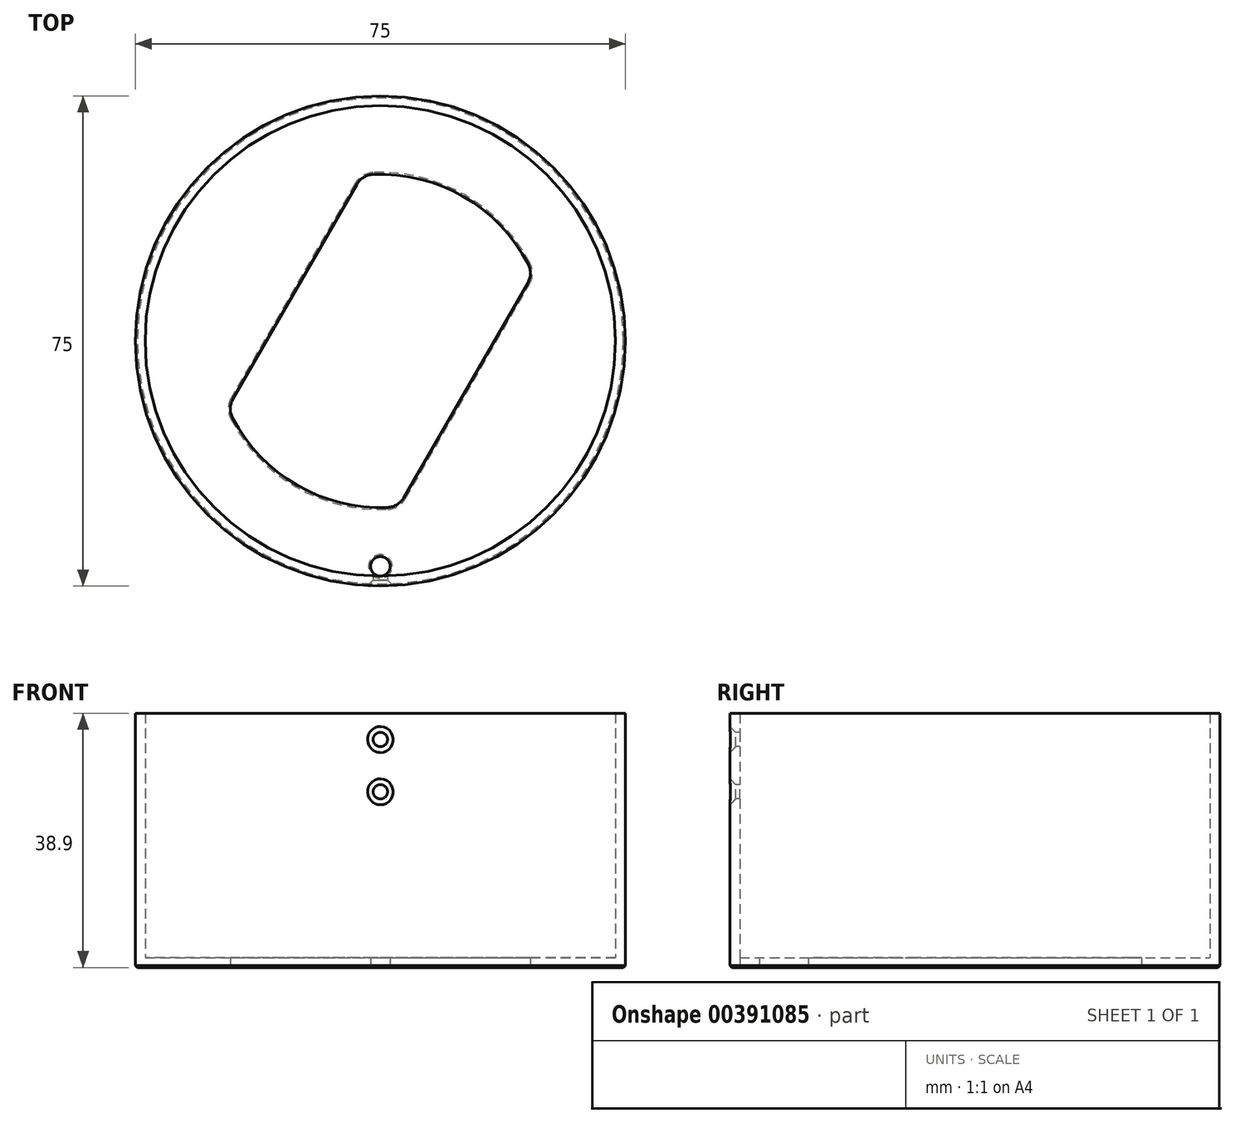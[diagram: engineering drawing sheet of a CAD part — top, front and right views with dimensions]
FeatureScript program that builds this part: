
annotation { "Feature Type Name" : "Feature", "Feature Type Description" : "" }
export const myFeature = defineFeature(function(context is Context, id is Id, definition is map)
    precondition{}
    {
        {
            var Q0;
            Q0=qCreatedBy(makeId("Top.planeOp"),FACE);
            var sketch = newSketch(context, id + "F0", { "sketchPlane" : qUnion([Q0])});
            skCircle(sketch, "E0", {"center": v(0, 0) * mm, "radius": 37.5 * mm});
            skCircle(sketch, "E1", {"center": v(0, 0) * mm, "radius": 36 * mm});
            skArc(sketch, "E2", {"start": v(-22.63, -11.76) * mm, "mid": v(-12.75, -22.08) * mm, "end": v(1.13, -25.48) * mm});
            skLineSegment(sketch, "E3", {"start": v(-29.66, -51.37) * mm, "end": v(37.36, 64.7) * mm, "construction": true});
            skLineSegment(sketch, "E4", {"start": v(-3.6, 23.98) * mm, "end": v(-22.56, -8.88) * mm});
            skLineSegment(sketch, "E5", {"start": v(3.6, -23.98) * mm, "end": v(22.56, 8.88) * mm});
            skArc(sketch, "E6.trimOffspring", {"start": v(22.63, 11.76) * mm, "mid": v(12.75, 22.08) * mm, "end": v(-1.13, 25.48) * mm});
            skPoint(sketch, "E7.visualSharp", {"position": v(-2.8, 25.35) * mm});
            skArc(sketch, "E7.filletArc", {"start": v(-1.13, 25.48) * mm, "mid": v(-2.55, 25.04) * mm, "end": v(-3.6, 23.98) * mm});
            skPoint(sketch, "E8.visualSharp", {"position": v(23.35, 10.25) * mm});
            skArc(sketch, "E8.filletArc", {"start": v(22.56, 8.88) * mm, "mid": v(22.96, 10.31) * mm, "end": v(22.63, 11.76) * mm});
            skPoint(sketch, "E9.visualSharp", {"position": v(2.8, -25.35) * mm});
            skArc(sketch, "E9.filletArc", {"start": v(1.13, -25.48) * mm, "mid": v(2.55, -25.04) * mm, "end": v(3.6, -23.98) * mm});
            skPoint(sketch, "E10.visualSharp", {"position": v(-23.35, -10.25) * mm});
            skArc(sketch, "E10.filletArc", {"start": v(-22.56, -8.88) * mm, "mid": v(-22.96, -10.31) * mm, "end": v(-22.63, -11.76) * mm});
            skPoint(sketch, "E11", {"position": v(0, -34.5) * mm});
            skCircle(sketch, "E12", {"center": v(0, -34.5) * mm, "radius": 1.5 * mm});
            skLineSegment(sketch, "E13", {"start": v(0, 0) * mm, "end": v(0, -37.5) * mm, "construction": true});
            skSolve(sketch);
        }
        {
            var Q0;
            Q0=makeQuery(id+"F0.imprint","IMPRINT",FACE,{"disambiguationData":[TD([[makeQuery(id+"F0.imprint","IMPRINT",EDGE,{"derivedFrom":sQuery(id+"F0.wireOp",EDGE,"E0")}),1.0]])]});
            extrude(context, id + "F1", {"entities" : qUnion([Q0]), "depth" : 38.9 * mm, "offsetDistance" : 25 * mm});
        }
        {
            var Q0;
            Q0 = qSketchRegion(id + "F0", true);
            var Q1;
            Q1=makeQuery(id+"F0.imprint","IMPRINT",FACE,{"disambiguationData":[TD([[makeQuery(id+"F0.imprint","IMPRINT",EDGE,{"derivedFrom":sQuery(id+"F0.wireOp",EDGE,"E1")}),1.0]])]});
            extrude(context, id + "F2", {"entities" : qUnion([Q0, Q1]), "operationType" : NewBodyOperationType.ADD, "depth" : 1.5 * mm, "offsetDistance" : 25 * mm});
        }
        {
            var Q0;
            Q0=sQuery(id+"F0.wireOp",EDGE,"E13");
            var Q1;
            Q1=sQuery(id+"F0.wireOp",VERTEX,"E13.end");
            cPlane(context, id + "F3", {"entities" : qUnion([Q0, Q1]), "cplaneType" : CPlaneType.LINE_POINT, "offset" : 25 * mm, "width" : 150 * mm, "height" : 150 * mm});
        }
        {
            var Q0;
            Q0=qCreatedBy(id+"F3.planeOp",FACE);
            var sketch = newSketch(context, id + "F4", { "sketchPlane" : qUnion([Q0])});
            skLineSegment(sketch, "E14.0", {"start": v(-37.5, 38.9) * mm, "end": v(37.5, 38.9) * mm});
            skPoint(sketch, "E15", {"position": v(0, 34.9) * mm});
            skPoint(sketch, "E15.positionSnap0", {"position": v(0, 38.9) * mm});
            skPoint(sketch, "E16", {"position": v(0, 26.9) * mm});
            skSolve(sketch);
        }
        {
            var Q0;
            Q0=sQuery(id+"F4.wireOp",VERTEX,"E15");
            var Q1;
            Q1=makeQuery(id+"F1.opExtrude","SWEPT_BODY",BODY,{"disambiguationData":[OSD([sQuery(id+"F0.wireOp",EDGE,"E0"),sQuery(id+"F0.wireOp",EDGE,"E1")])]});
            hole(context, id + "F5", {"style" : HoleStyle.C_SINK, "endStyle" : HoleEndStyle.BLIND, "holeDiameter" : 2.2 * mm, "cSinkDiameter" : 4 * mm, "cSinkAngle" : 90 * degree, "holeDepth" : 11 * mm, "isTappedThrough" : true, "tappedDepth" : 100 * mm, "tapClearance" : 3, "startFromSketch" : true, "locations" : qUnion([Q0]), "scope" : qUnion([Q1])});
        }
        {
            var Q0;
            Q0=sQuery(id+"F4.wireOp",VERTEX,"E16");
            var Q1;
            Q1=makeQuery(id+"F1.opExtrude","SWEPT_BODY",BODY,{"disambiguationData":[OSD([sQuery(id+"F0.wireOp",EDGE,"E0"),sQuery(id+"F0.wireOp",EDGE,"E1")])]});
            hole(context, id + "F6", {"style" : HoleStyle.C_SINK, "endStyle" : HoleEndStyle.BLIND, "holeDiameter" : 2.2 * mm, "cSinkDiameter" : 4 * mm, "cSinkAngle" : 90 * degree, "holeDepth" : 11 * mm, "isTappedThrough" : true, "tappedDepth" : 100 * mm, "tapClearance" : 3, "startFromSketch" : true, "locations" : qUnion([Q0]), "scope" : qUnion([Q1])});
        }
        {
            var Q0;
            Q0=makeQuery(id+"F1.opExtrude","CAP_EDGE",EDGE,{"disambiguationData":[OSD([sQuery(id+"F0.wireOp",EDGE,"E0")])],"isStart":true});
            var Q1;
            Q1=makeQuery(id+"F2.opExtrude","CAP_EDGE",EDGE,{"disambiguationData":[OSD([sQuery(id+"F0.wireOp",EDGE,"E6.trimOffspring")])],"isStart":true});
            var Q2;
            Q2=makeQuery(id+"F2.opExtrude","CAP_EDGE",EDGE,{"disambiguationData":[OSD([sQuery(id+"F0.wireOp",EDGE,"E12")])],"isStart":true});
            chamfer(context, id + "F7", {"entities" : qUnion([Q0, Q1, Q2]), "width" : .3 * mm, "tangentPropagation" : true});
        }
    });
